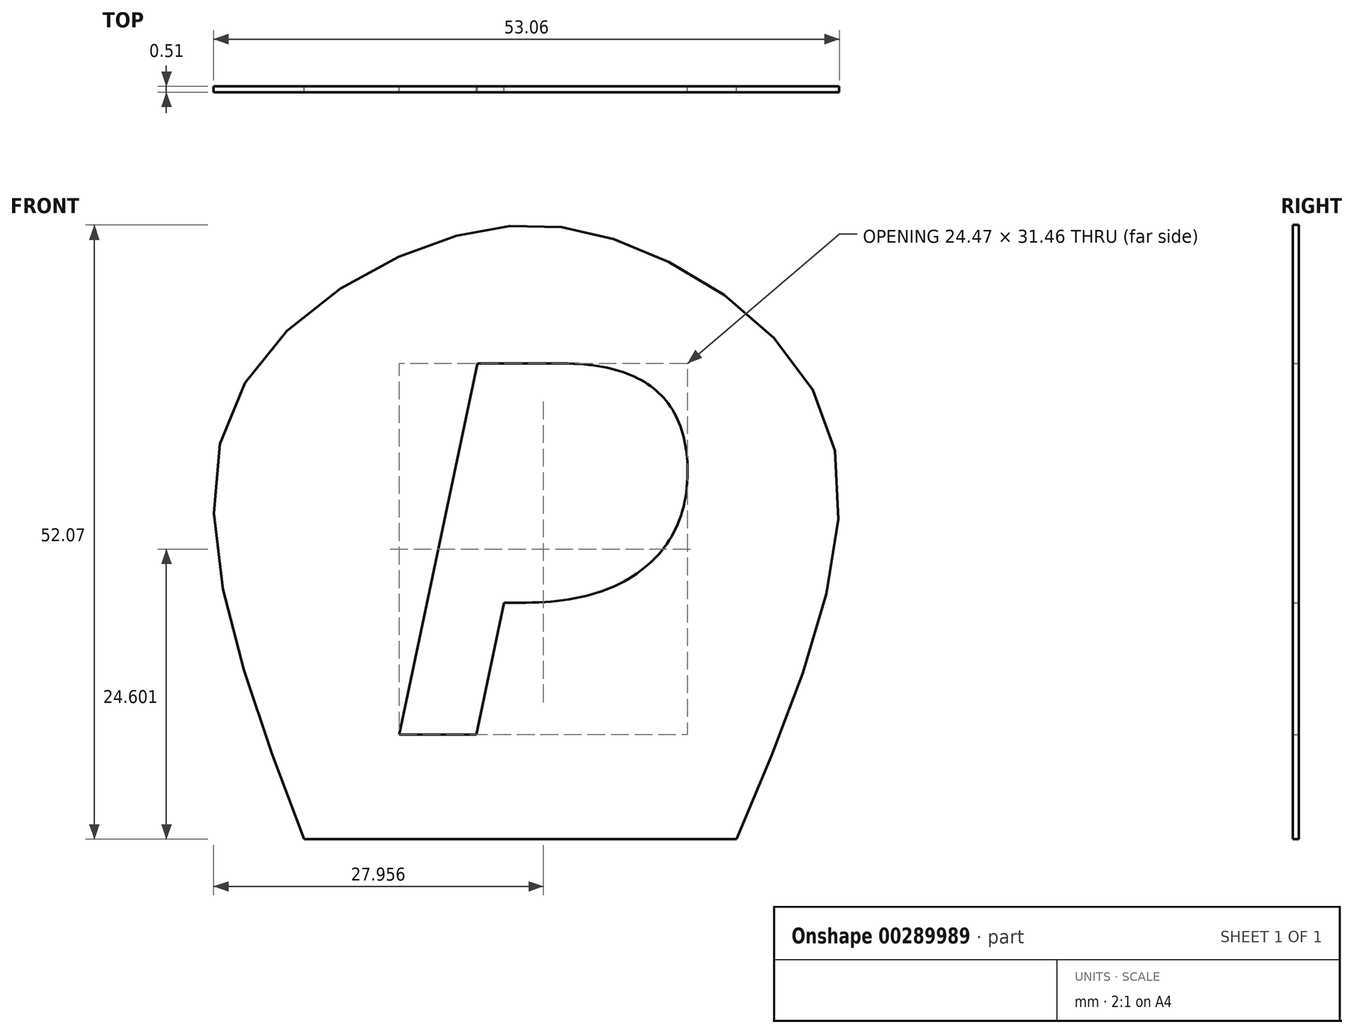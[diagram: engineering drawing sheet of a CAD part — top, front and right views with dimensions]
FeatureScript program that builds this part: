
annotation { "Feature Type Name" : "Feature", "Feature Type Description" : "" }
export const myFeature = defineFeature(function(context is Context, id is Id, definition is map)
    precondition{}
    {
        {
            var Q0;
            Q0=qCreatedBy(makeId("Front.planeOp"),FACE);
            var sketch = newSketch(context, id + "F0", { "sketchPlane" : qUnion([Q0])});
            skLineSegment(sketch, "E0", {"start": v(-21.09, -18.72) * mm, "end": v(-14.78, -18.72) * mm});
            skLineSegment(sketch, "E1", {"start": v(-14.78, -18.72) * mm, "end": v(15.57, -18.72) * mm});
            skFitSpline(sketch, "E2", {"points": [v(15.57, -18.72) * mm, v(23.45, 16.16) * mm, v(6.9, 31.53) * mm, v(-9.26, 32.12) * mm, v(-27.59, 16.95) * mm, v(-21.09, -18.72) * mm], "startDerivative": vector(69.71, 164.1) * mm, "endDerivative": vector(64.07, -167.47) * mm});
            skText(sketch, "E3", { "text": "P", "fontName": "OpenSans-BoldItalic.ttf"});
            const initialGuessF0  = {"E3": [-0.01419, -0.00985, 1, 0, 0.03173]};
            skSetInitialGuess(sketch, initialGuessF0);
            skSolve(sketch);
        }
        {
            var Q0;
            Q0 = qSketchRegion(id + "F0", true);
            extrude(context, id + "F1", {"entities" : qUnion([Q0]), "depth" : 0.5 * mm});
        }
    });
